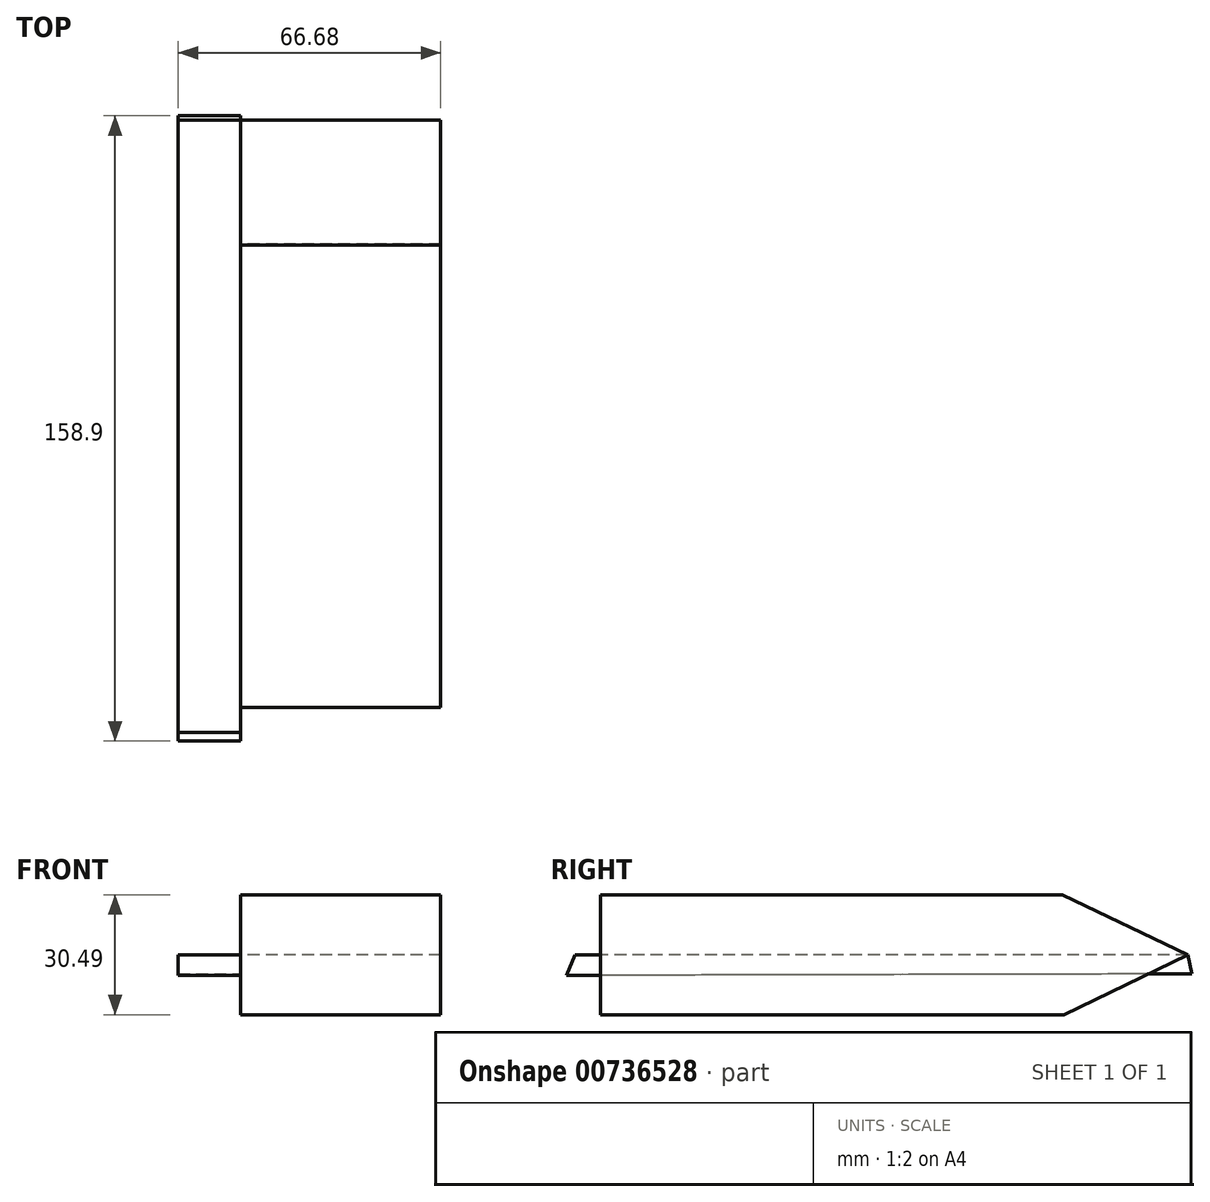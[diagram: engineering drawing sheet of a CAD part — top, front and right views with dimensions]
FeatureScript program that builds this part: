
annotation { "Feature Type Name" : "Feature", "Feature Type Description" : "" }
export const myFeature = defineFeature(function(context is Context, id is Id, definition is map)
    precondition{}
    {
        {
            var Q0;
            Q0=qCreatedBy(makeId("Right.planeOp"),FACE);
            var sketch = newSketch(context, id + "F0", { "sketchPlane" : qUnion([Q0])});
            skLineSegment(sketch, "E0", {"start": v(-78.45, 7.23) * mm, "end": v(-78.45, 22.48) * mm});
            skLineSegment(sketch, "E1", {"start": v(-78.45, 22.48) * mm, "end": v(39.03, 22.48) * mm});
            skLineSegment(sketch, "E2", {"start": v(39.03, 22.48) * mm, "end": v(70.78, 7.23) * mm});
            skLineSegment(sketch, "E3", {"start": v(-78.45, 7.23) * mm, "end": v(-78.45, -8.01) * mm});
            skLineSegment(sketch, "E4", {"start": v(-78.45, -8.01) * mm, "end": v(39.3, -8.01) * mm});
            skLineSegment(sketch, "E5", {"start": v(39.3, -8.01) * mm, "end": v(70.78, 7.23) * mm});
            skSolve(sketch);
        }
        {
            var Q0;
            Q0 = qSketchRegion(id + "F0", true);
            extrude(context, id + "F1", {"entities" : qUnion([Q0]), "depth" : 50.8 * mm, "offsetDistance" : 25.4 * mm});
        }
        {
            var Q0;
            Q0=qCreatedBy(makeId("Right.planeOp"),FACE);
            var sketch = newSketch(context, id + "F2", { "sketchPlane" : qUnion([Q0])});
            skLineSegment(sketch, "E6", {"start": v(70.78, 7.24) * mm, "end": v(-78.45, 7.24) * mm});
            skLineSegment(sketch, "E7", {"start": v(-78.45, 7.24) * mm, "end": v(-84.8, 7.24) * mm});
            skLineSegment(sketch, "E8", {"start": v(-84.8, 7.24) * mm, "end": v(-87, 1.95) * mm});
            skLineSegment(sketch, "E9", {"start": v(70.78, 7.24) * mm, "end": v(71.9, 2.34) * mm});
            skLineSegment(sketch, "E10", {"start": v(71.9, 2.34) * mm, "end": v(-87, 1.95) * mm});
            skSolve(sketch);
        }
        {
            var Q0;
            Q0 = qSketchRegion(id + "F2", true);
            extrude(context, id + "F3", {"entities" : qUnion([Q0]), "operationType" : NewBodyOperationType.ADD, "oppositeDirection" : true, "depth" : 15.88 * mm, "offsetDistance" : 25.4 * mm});
        }
    });
